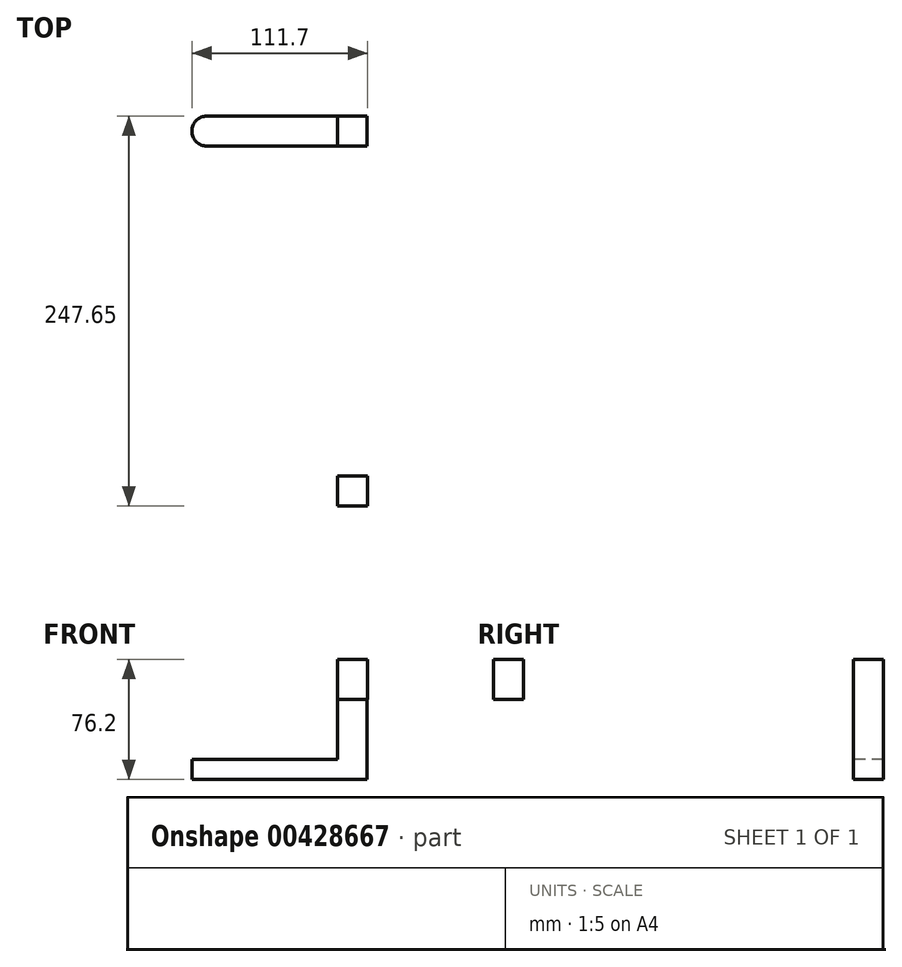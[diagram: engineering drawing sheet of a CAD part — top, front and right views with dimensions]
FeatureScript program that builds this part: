
annotation { "Feature Type Name" : "Feature", "Feature Type Description" : "" }
export const myFeature = defineFeature(function(context is Context, id is Id, definition is map)
    precondition{}
    {
        {
            var Q0;
            Q0=qCreatedBy(makeId("Top.planeOp"),FACE);
            var sketch = newSketch(context, id + "F0", { "sketchPlane" : qUnion([Q0])});
            skLineSegment(sketch, "E0.bottom", {"start": v(-48.98, 9.53) * mm, "end": v(52.62, 9.53) * mm});
            skLineSegment(sketch, "E0.top", {"start": v(-48.98, -9.53) * mm, "end": v(52.62, -9.53) * mm});
            skPoint(sketch, "E0.middle", {"position": v(1.82, 0) * mm});
            skLineSegment(sketch, "E1", {"start": v(34.15, -9.52) * mm, "end": v(34.15, 9.53) * mm});
            skLineSegment(sketch, "E2", {"start": v(52.62, 9.53) * mm, "end": v(52.62, -9.53) * mm});
            skArc(sketch, "E3", {"start": v(-48.98, 9.53) * mm, "mid": v(-58.5, 0) * mm, "end": v(-48.98, -9.53) * mm});
            skSolve(sketch);
        }
        {
            var Q0;
            Q0=makeQuery(id+"F0.imprint","IMPRINT",FACE,{"disambiguationData":[TD([[makeQuery(id+"F0.imprint","IMPRINT",EDGE,{"derivedFrom":sQuery(id+"F0.wireOp",EDGE,"E0.bottom")}),-1.0]])]});
            var Q1;
            Q1=makeQuery(id+"F0.imprint","IMPRINT",FACE,{"disambiguationData":[TD([[makeQuery(id+"F0.imprint","IMPRINT",EDGE,{"derivedFrom":sQuery(id+"F0.wireOp",EDGE,"a23YLQUS-zPUK-Y7R4-v89D-SNyPPI4aXNRm.top")}),1.0]])]});
            var Q2;
            {var subQ3=sQuery(id+"F0.wireOp",EDGE,"E0.right");var subQ7=makeQuery(id+"F0.imprint","IMPRINT",EDGE,{"derivedFrom":subQ3});Q2=makeQuery(id+"FttVHyuVe9vGC4O_0.imprint","IMPRINT",FACE,{"disambiguationData":[TD([[makeQuery(id+"FttVHyuVe9vGC4O_0.imprint","IMPRINT",EDGE,{"derivedFrom":subQ7}),1.0]])]});}
            extrude(context, id + "F1", {"entities" : qUnion([Q0, Q1, Q2]), "depth" : 12.7 * mm});
        }
        {
            var Q0;
            {var subQ0=sQuery(id+"F0.wireOp",EDGE,"E0.left");Q0=makeQuery(id+"F0.imprint","IMPRINT",FACE,{"disambiguationData":[TD([[makeQuery(id+"F0.imprint","IMPRINT",EDGE,{"derivedFrom":subQ0}),1.0]])]});}
            var Q1;
            {var subQ2=sQuery(id+"F0.wireOp",EDGE,"E1");Q1=makeQuery(id+"F0.imprint","IMPRINT",FACE,{"disambiguationData":[TD([[makeQuery(id+"F0.imprint","IMPRINT",EDGE,{"derivedFrom":subQ2}),-1.0]])]});}
            extrude(context, id + "F2", {"entities" : qUnion([Q0, Q1]), "operationType" : NewBodyOperationType.ADD, "depth" : 76.2 * mm});
        }
        {
            var Q0;
            Q0=makeQuery(id+"F2.opExtrude","CAP_FACE",FACE,{"disambiguationData":[OSD([sQuery(id+"F0.wireOp",EDGE,"E0.bottom"),sQuery(id+"F0.wireOp",EDGE,"E0.top"),sQuery(id+"F0.wireOp",EDGE,"E0.left"),sQuery(id+"F0.wireOp",EDGE,"E1")])],"isStart":false});
            var sketch = newSketch(context, id + "F3", { "sketchPlane" : qUnion([Q0])});
            skLineSegment(sketch, "E4.bottom", {"start": v(34.15, -9.53) * mm, "end": v(53.2, -9.53) * mm});
            skLineSegment(sketch, "E4.top", {"start": v(34.15, -238.13) * mm, "end": v(53.2, -238.13) * mm});
            skLineSegment(sketch, "E4.left", {"start": v(34.15, -9.53) * mm, "end": v(34.15, -238.13) * mm});
            skLineSegment(sketch, "E4.right", {"start": v(53.2, -9.53) * mm, "end": v(53.2, -238.13) * mm});
            skLineSegment(sketch, "E5.top", {"start": v(34.15, -219.08) * mm, "end": v(53.2, -219.08) * mm});
            skLineSegment(sketch, "E5.left", {"start": v(34.15, -238.13) * mm, "end": v(34.15, -219.08) * mm});
            skLineSegment(sketch, "E5.right", {"start": v(53.2, -238.13) * mm, "end": v(53.2, -219.08) * mm});
            skSolve(sketch);
        }
        {
            var Q0;
            {var subQ1=sQuery(id+"F3.wireOp",EDGE,"E4.left");Q0=makeQuery(id+"F3.imprint","IMPRINT",FACE,{"disambiguationData":[TD([[makeQuery(id+"F3.imprint","IMPRINT",EDGE,{"derivedFrom":subQ1}),1.0]])]});}
            extrude(context, id + "F4", {"entities" : qUnion([Q0]), "operationType" : NewBodyOperationType.ADD, "oppositeDirection" : true, "depth" : 12.7 * mm});
        }
        {
            var Q0;
            Q0=makeQuery(id+"F3.imprint","IMPRINT",FACE,{"disambiguationData":[TD([[makeQuery(id+"F3.imprint","IMPRINT",EDGE,{"derivedFrom":sQuery(id+"F3.wireOp",EDGE,"0VAypezG-u6De-hI7b-lwNC-UiBgYS2O4OOY.bottom")}),1.0]])]});
            var Q1;
            Q1=makeQuery(id+"F3.imprint","IMPRINT",FACE,{"disambiguationData":[TD([[makeQuery(id+"F3.imprint","IMPRINT",EDGE,{"derivedFrom":sQuery(id+"F3.wireOp",EDGE,"E4.top")}),1.0]])]});
            extrude(context, id + "F5", {"entities" : qUnion([Q0, Q1]), "operationType" : NewBodyOperationType.ADD, "oppositeDirection" : true, "depth" : 25.4 * mm});
        }
        {
            var Q0;
            Q0=makeQuery(id+"F1.opExtrude","SWEPT_BODY",BODY,{"disambiguationData":[OSD([sQuery(id+"F0.wireOp",EDGE,"E0.bottom"),sQuery(id+"F0.wireOp",EDGE,"E0.top"),sQuery(id+"F0.wireOp",EDGE,"E0.left"),sQuery(id+"F0.wireOp",EDGE,"iKiLxKRv-E8Ol-8Jty-5MgC-1inANsQ0tGW4")])]});
            transform(context, id + "F6", {"entities" : qUnion([Q0]), "transformType" : TransformType.TRANSLATION_3D, "dx" : 0 * mm, "dy" : 0 * mm, "dz" : 0 * mm, "makeCopy" : true});
        }
        {
            var Q0;
            Q0=makeQuery(id+"F6.opPattern","COPY",BODY,{"derivedFrom":makeQuery(id+"F1.opExtrude","SWEPT_BODY",BODY,{"disambiguationData":[OSD([sQuery(id+"F0.wireOp",EDGE,"E0.bottom"),sQuery(id+"F0.wireOp",EDGE,"E0.top"),sQuery(id+"F0.wireOp",EDGE,"E0.left"),sQuery(id+"F0.wireOp",EDGE,"iKiLxKRv-E8Ol-8Jty-5MgC-1inANsQ0tGW4")])]}),"instanceName":"1"});
            deleteBodies(context, id + "F7", {"entities" : qUnion([Q0])});
        }
    });
